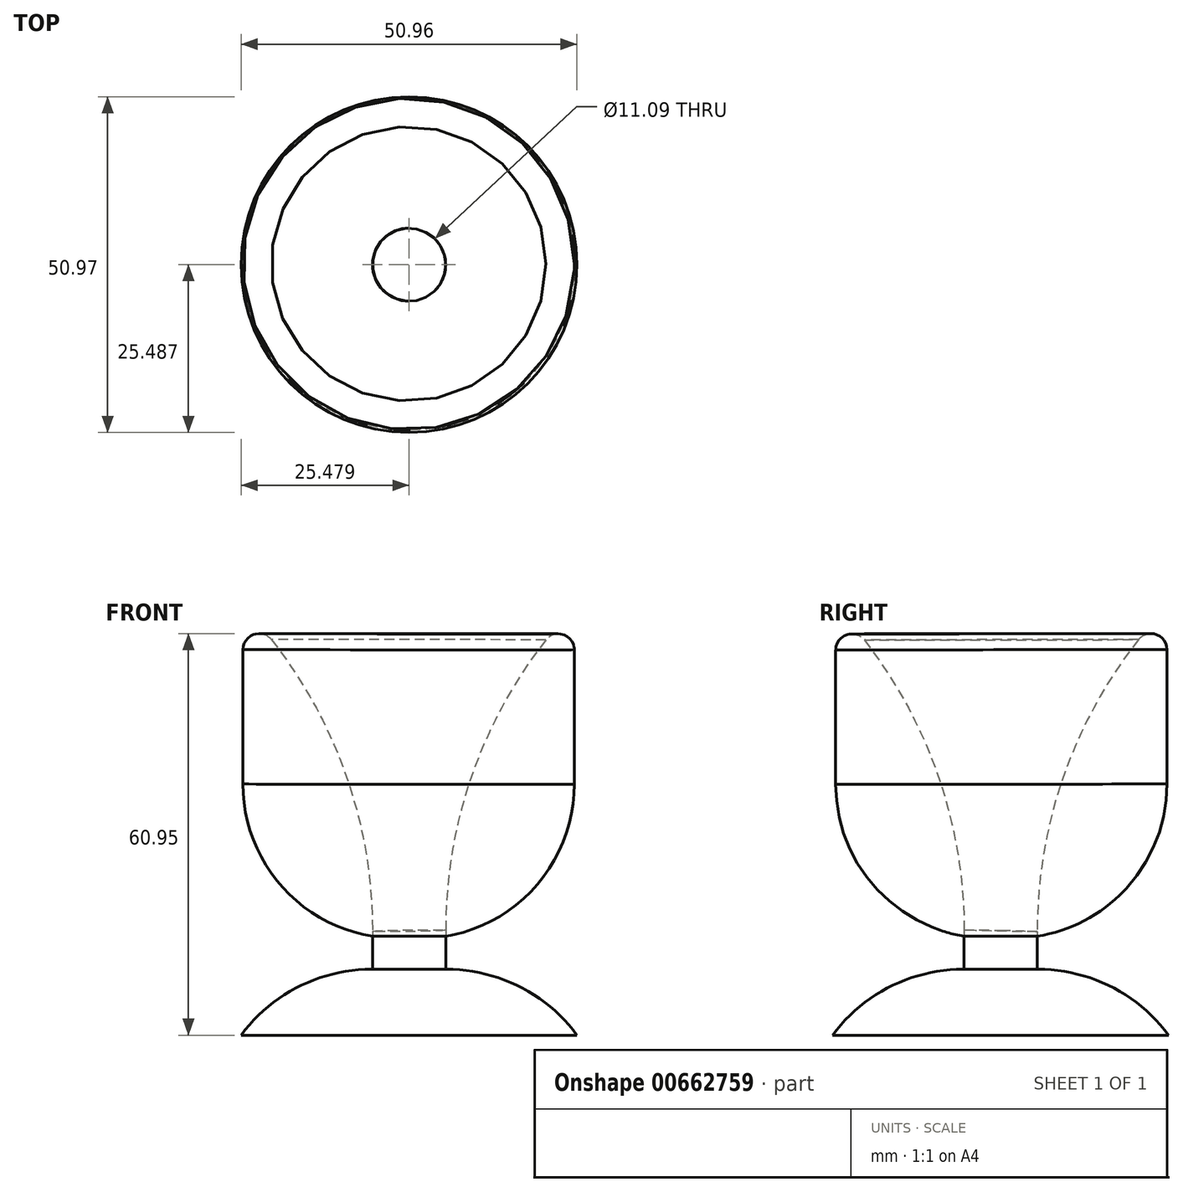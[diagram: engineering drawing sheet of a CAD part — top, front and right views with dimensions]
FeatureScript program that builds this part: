
annotation { "Feature Type Name" : "Feature", "Feature Type Description" : "" }
export const myFeature = defineFeature(function(context is Context, id is Id, definition is map)
    precondition{}
    {
        {
            var Q0;
            Q0=qCreatedBy(makeId("Top.planeOp"),FACE);
            var sketch = newSketch(context, id + "F0", { "sketchPlane" : qUnion([Q0])});
            skCircle(sketch, "E0", {"center": v(-26.75, 14.89) * mm, "radius": 25.48 * mm});
            skSolve(sketch);
        }
        {
            var Q0;
            Q0=makeQuery(id+"F0.imprint","IMPRINT",FACE,{"disambiguationData":[TD([[makeQuery(id+"F0.imprint","IMPRINT",EDGE,{"derivedFrom":sQuery(id+"F0.wireOp",EDGE,"E0")}),1.0]])]});
            extrude(context, id + "F1", {"entities" : qUnion([Q0]), "depth" : 10 * mm, "offsetDistance" : 25 * mm});
        }
        {
            var Q0;
            Q0=makeQuery(id+"F1.opExtrude","CAP_EDGE",EDGE,{"disambiguationData":[OSD([sQuery(id+"F0.wireOp",EDGE,"E0")])],"isStart":false});
            fillet(context, id + "F2", {"entities" : qUnion([Q0]), "radius" : 24.62 * mm, "tangentPropagation" : true, "allowEdgeOverflow" : false});
        }
        {
            var Q0;
            Q0=makeQuery(id+"F1.opExtrude","CAP_FACE",FACE,{"disambiguationData":[OSD([sQuery(id+"F0.wireOp",EDGE,"E0")])],"isStart":false});
            var sketch = newSketch(context, id + "F3", { "sketchPlane" : qUnion([Q0])});
            skCircle(sketch, "E1", {"center": v(-26.75, 14.89) * mm, "radius": 5.55 * mm});
            skSolve(sketch);
        }
        {
            var Q0;
            Q0=makeQuery(id+"F3.imprint","IMPRINT",FACE,{"disambiguationData":[TD([[makeQuery(id+"F3.imprint","IMPRINT",EDGE,{"derivedFrom":sQuery(id+"F3.wireOp",EDGE,"E1")}),1.0]])]});
            extrude(context, id + "F4", {"entities" : qUnion([Q0]), "operationType" : NewBodyOperationType.ADD, "depth" : 5 * mm, "offsetDistance" : 25 * mm});
        }
        {
            var Q0;
            Q0=makeQuery(id+"F4.opExtrude","CAP_FACE",FACE,{"disambiguationData":[OSD([sQuery(id+"F3.wireOp",EDGE,"E1")])],"isStart":false});
            var sketch = newSketch(context, id + "F5", { "sketchPlane" : qUnion([Q0])});
            skSolve(sketch);
        }
        {
            var Q0;
            Q0=makeQuery(id+"F5.imprint","IMPRINT",FACE,{"disambiguationData":[TD([[makeQuery(id+"F5.imprint","IMPRINT",EDGE,{"derivedFrom":makeQuery(id+"F4.opExtrude","CAP_EDGE",EDGE,{"disambiguationData":[OSD([sQuery(id+"F3.wireOp",EDGE,"E1")])],"isStart":false})}),1.0]])]});
            var sketch = newSketch(context, id + "F6", { "sketchPlane" : qUnion([Q0])});
            skCircle(sketch, "E2", {"center": v(-26.82, 15) * mm, "radius": 25.13 * mm});
            skSolve(sketch);
        }
        {
            var Q0;
            Q0=makeQuery(id+"F6.imprint","IMPRINT",FACE,{"disambiguationData":[TD([[makeQuery(id+"F6.imprint","IMPRINT",EDGE,{"derivedFrom":sQuery(id+"F6.wireOp",EDGE,"E2")}),1.0]])]});
            extrude(context, id + "F7", {"entities" : qUnion([Q0]), "depth" : 50 * mm, "offsetDistance" : 25 * mm});
        }
        {
            var Q0;
            Q0=makeQuery(id+"F7.opExtrude","CAP_EDGE",EDGE,{"disambiguationData":[OSD([sQuery(id+"F3.wireOp",EDGE,"E1")])],"isStart":false});
            fillet(context, id + "F8", {"entities" : qUnion([Q0]), "radius" : 71.46 * mm, "tangentPropagation" : true, "allowEdgeOverflow" : false});
        }
        {
            var Q0;
            Q0=makeQuery(id+"F7.opExtrude","CAP_EDGE",EDGE,{"disambiguationData":[OSD([sQuery(id+"F6.wireOp",EDGE,"E2")])],"isStart":true});
            fillet(context, id + "F9", {"entities" : qUnion([Q0]), "radius" : 23.42 * mm, "tangentPropagation" : true, "allowEdgeOverflow" : false});
        }
        {
            var Q0;
            Q0=makeQuery(id+"F8.opFillet","BLEND_EDGE",EDGE,{"blendedFrom":[makeQuery(id+"F7.opExtrude","CAP_EDGE",EDGE,{"disambiguationData":[OSD([sQuery(id+"F3.wireOp",EDGE,"E1")])],"isStart":false}),makeQuery(id+"F7.opExtrude","SWEPT_FACE",FACE,{"disambiguationData":[OSD([sQuery(id+"F6.wireOp",EDGE,"E2")])]})],"blendedInto":[makeQuery(id+"F7.opExtrude","SWEPT_FACE",FACE,{"disambiguationData":[OSD([sQuery(id+"F6.wireOp",EDGE,"E2")])]})]});
            fillet(context, id + "F10", {"entities" : qUnion([Q0]), "radius" : 2.42 * mm, "tangentPropagation" : true, "allowEdgeOverflow" : false});
        }
    });
